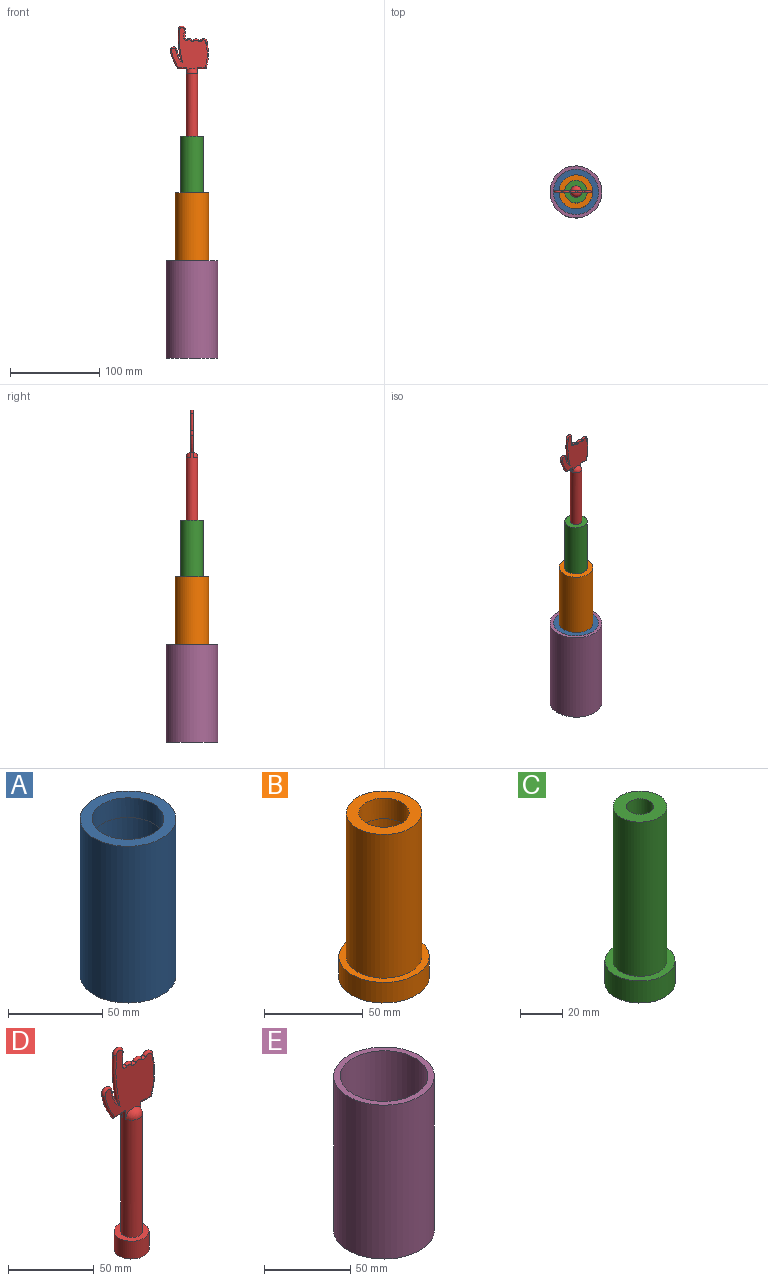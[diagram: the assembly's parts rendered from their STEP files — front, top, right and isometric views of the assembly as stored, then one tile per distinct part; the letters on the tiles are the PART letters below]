
ASSEMBLY  parts=5 mates=4
PART A: 6 faces, bbox 50.8x50.8x101.6 mm
  f0: cylinder r=19.05mm len=38.1mm, axis (0,0,1), area 1520.1mm2, adj f2,f4
  f1: cylinder r=25.4mm len=101.6mm, axis (0,0,-1), area 16214.6mm2, adj f2,f3
  f2: plane 50.8x50.8mm, normal (0,0,1), area 886.7mm2, adj f0,f1
  f3: plane 50.8x50.8mm, normal (0,0,-1), area 385.1mm2, adj f1,f5
  f4: plane 45.72x45.72mm, normal (0,0,-1), area 501.6mm2, adj f0,f5
  f5: cylinder r=22.86mm len=88.9mm, axis (0,0,-1), area 12769mm2, adj f3,f4
PART B: 8 faces, bbox 45.7x45.7x101.6 mm
  f0: cylinder r=12.7mm len=25.4mm, axis (0,0,1), area 1013.4mm2, adj f2,f7
  f1: cylinder r=19.05mm len=88.9mm, axis (0,0,-1), area 10640.9mm2, adj f2,f5
  f2: plane 38.1x38.1mm, normal (0,0,1), area 633.4mm2, adj f0,f1
  f3: cylinder r=22.86mm len=45.72mm, axis (0,0,1), area 1824.1mm2, adj f4,f5
  f4: plane 45.72x45.72mm, normal (0,0,-1), area 785.4mm2, adj f3,f6
  f5: plane 45.72x45.72mm, normal (0,0,1), area 501.6mm2, adj f1,f3
  f6: cylinder r=16.51mm len=88.9mm, axis (0,0,-1), area 9222.1mm2, adj f4,f7
  f7: plane 33.02x33.02mm, normal (0,0,-1), area 349.6mm2, adj f0,f6
PART C: 8 faces, bbox 33x33x101.6 mm
  f0: cylinder r=6.35mm len=12.7mm, axis (0,0,-1), area 506.7mm2, adj f2,f4
  f1: cylinder r=12.7mm len=88.9mm, axis (0,0,-1), area 7093.9mm2, adj f2,f5
  f2: plane 25.4x25.4mm, normal (0,0,1), area 380mm2, adj f0,f1
  f3: cylinder r=10.16mm len=88.9mm, axis (0,0,-1), area 5675.1mm2, adj f4,f6
  f4: plane 20.32x20.32mm, normal (0,0,-1), area 197.6mm2, adj f0,f3
  f5: plane 33.02x33.02mm, normal (0,0,1), area 349.6mm2, adj f1,f7
  f6: plane 33.02x33.02mm, normal (0,0,-1), area 532mm2, adj f3,f7
  f7: cylinder r=16.51mm len=33.02mm, axis (0,0,1), area 1317.4mm2, adj f5,f6
PART D: 24 faces, bbox 51x20.3x149.8 mm
  f0: plane 51.7x40.3mm, normal (0,-1,0), area 1104mm2, adj f2,f6,f7,f8,f9,f10,f11,f12
  f1: plane 51.7x40.3mm, normal (0,1,0), area 1104mm2, adj f2,f6,f7,f8,f9,f10,f11,f12
  f2: cylinder r=6.35mm len=90.17mm, axis (0,0,-1), area 3373.5mm2, adj f0,f1,f5,f6,f20,f22,f23
  f3: cylinder r=10.16mm len=20.32mm, axis (0,0,1), area 810.7mm2, adj f4,f5
  f4: plane 20.32x20.32mm, normal (0,0,-1), area 324.3mm2, adj f3
  f5: plane 20.32x20.32mm, normal (0,0,1), area 197.6mm2, adj f2,f3
  f6: cylinder r=1.27mm len=9.59mm, axis (1,0,0), area 36.2mm2, adj f0,f1,f2,f7
  f7: torus R=50.72mm, axis (0,-1,0), area 112.6mm2, adj f0,f1,f6,f8
  f8: torus R=2.54mm, axis (0,-1,0), area 2.4mm2, adj f0,f1,f7,f9
  f9: torus R=2.87mm, axis (0,-1,0), area 37.7mm2, adj f0,f1,f8,f10
  f10: torus R=2.54mm, axis (0,-1,0), area 11.9mm2, adj f0,f1,f9,f11
  f11: torus R=2.92mm, axis (0,-1,0), area 24.7mm2, adj f0,f1,f10,f12
  f12: torus R=2.54mm, axis (0,-1,0), area 12mm2, adj f0,f1,f11,f13
  f13: torus R=2.84mm, axis (0,-1,0), area 21.4mm2, adj f0,f1,f12,f14
  f14: torus R=2.54mm, axis (0,-1,0), area 14.6mm2, adj f0,f1,f13,f15
  f15: torus R=286.09mm, axis (0,-1,0), area 38mm2, adj f0,f1,f14,f16
  f16: torus R=2.54mm, axis (0,-1,0), area 42.5mm2, adj f0,f1,f15,f17
  f17: torus R=117.36mm, axis (0,-1,0), area 143.1mm2, adj f0,f1,f16,f18
  f18: torus R=22.37mm, axis (0,-1,0), area 52.4mm2, adj f0,f1,f17,f19
  f19: torus R=2.54mm, axis (0,-1,0), area 45.9mm2, adj f0,f1,f18,f21
  f20: cylinder r=1.27mm len=9.59mm, axis (1,0,0), area 36.7mm2, adj f0,f1,f2,f21
  f21: torus R=48.15mm, axis (0,-1,0), area 83.5mm2, adj f0,f1,f19,f20
  f22: torus R=1.27mm, axis (0,0,1), area 92mm2, adj f0,f2
  f23: torus R=1.27mm, axis (0,0,1), area 92mm2, adj f1,f2
PART E: 5 faces, bbox 58.4x58.4x109.2 mm
  f0: cylinder r=25.4mm len=101.6mm, axis (0,0,1), area 16214.6mm2, adj f1,f2
  f1: plane 50.8x50.8mm, normal (0,0,1), area 2026.8mm2, adj f0
  f2: plane 58.42x58.42mm, normal (0,0,1), area 653.7mm2, adj f0,f4
  f3: plane 58.42x58.42mm, normal (0,0,-1), area 2680.5mm2, adj f4
  f4: cylinder r=29.21mm len=109.22mm, axis (0,0,-1), area 20045.3mm2, adj f2,f3
PLACE A rot(axis=(0,0,1),0deg) t=(405.27,-482.05,-1584.35)mm
PLACE B rot(axis=(0,0,1),0deg) t=(405.27,-482.05,-1508.15)mm
PLACE C rot(axis=(0,0,1),0deg) t=(405.27,-482.05,-1444.65)mm
PLACE D rot(axis=(0,0,1),0deg) t=(405.27,-482.05,-1355.75)mm
PLACE E rot(axis=(0,0,1),0deg) t=(405.27,-482.05,-1591.97)mm
MATE slider C.f7 <-> B.f6  axis (0,0,-1) through (405.27,-482.05,-1444.65)mm
MATE slider B.f3 <-> A.f5  axis (0,0,-1) through (405.27,-482.05,-1508.15)mm
MATE slider D.f3 <-> C.f3  axis (0,0,1) through (405.27,-482.05,-1355.75)mm
MATE fastened A.f1 <-> E.f0  axis (0,0,-1) through (405.27,-482.05,-1584.35)mm
